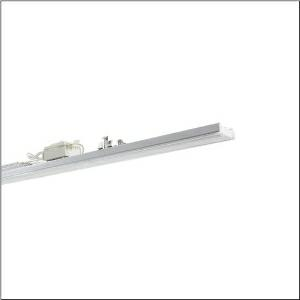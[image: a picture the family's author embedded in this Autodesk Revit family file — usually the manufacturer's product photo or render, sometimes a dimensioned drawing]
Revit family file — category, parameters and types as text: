
# Revit family: licross_r__11_recessed_mo_51tl14dn425g_84cd
name_source: partatom
category: Lighting Fixtures
units: mm (PartAtom-declared; Revit-internal decimal feet)

## family parameters
Cut with Voids When Loaded = No
Host = Face
Light Source = No
Part Type = Normal
Room Calculation Point = No
Round Connector Dimension = Use Diameter
Shared = No

## types (1)
- --- (1 x LED, 2600 lm, 15.2 W, 4000K)
    Apparent Load = 15 VA
    CIE Flux Codes = 56 84 97 100 100
    Color Rendering = 80
    Color Temperature = 4000K
    Default Elevation = 1800 mm
    Description = Licross® 11 Recessed MO, luminaire insert, of sheet steel, coil coated, white, length: 1.500mm, width: 66mm, height: 67mm, LED rated luminous flux: 2.600lm, light colour: 840, control gear: DALI 2, with plug, 5-pole, with phase selection, mains connection: 220..240V, AC, 50/60Hz, rated input power: 15.2W, internal wiring halogen-free, primary light control with lens, of plastic, primary optical cover: cover, of PMMA, light emission: direct distribution, primary light characteristic: asymmetric, protection rating (complete): IP40, insulation class (complete): insulation class I (protective earthing), certification: CE, ENEC, VDE, UKCA, protection symbol: D if used in an environment without relevant dust loads with corresponding accessories, impact resistance: IK06, permissible ambient temperature for indoor applications: -25..+50°C, corresponds to IFS (International Featured Standards) requirements for safety and quality in the food industry, reducing of maximum allowable ambient temperature of 5°C with ceiling mounting, LABS conformity tested according to VDMA 24364:2018-05, packaging unit: 1 piece
    Height = 58 mm
    Lamp = 1 x LED
    Lamp Light Flux = 2600 lm
    Lamp Power = 15.2 W
    Lamp count = 1
    Length = 1500 mm
    Luminous efficacy = 171 lm/W
    Manufacturer = Siteco
    ModVariant = No
    Model = 51TL14DN425G
    Mounting Place = Ceiling
    Mounting Type = Pendant
    Number of Poles = 1
    OnlyDefault = Yes
    Power Factor = 1
    Product Name = Licross® 11 Recessed MO
    Product group = luminaire insert | ceiling pendant
    ProductGroupID = 902
    Protection Class = Protection class I
    Protection Degree = IP 40
    RLX_Detail_Level = 1
    RLX_Emergency_Light_Flux = 0 lm
    RLX_Emergency_Type = 0
    RLX_Emergency_Type_DB = No
    RlxData = <blob elided: 24273 chars, md5=fc89b0ae>
    Socket = socket
    Standby Power = 0 W
    System Light Flux = 2600 lm
    System Power = 15 W
    Type Comments = factory setting: luminous flux: 100 % | dim-lin: 254 | 98 mA
    Type Image = l_1296930.jpg
    URL = http://relux.com
    VarID = @adj_089189
    Voltage = 0 V
    Weight = 0.00 kg
    Width = 66 mm

## geometry (parser evidence)
native form markers: Blend x4, Sweep x13
no freeform markers — native parametric forms only
